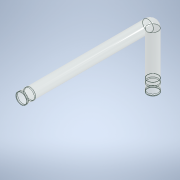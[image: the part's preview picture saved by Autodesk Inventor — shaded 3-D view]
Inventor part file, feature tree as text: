
AUTODESK INVENTOR PART (.ipt)
format: ipt  version: 2020 (Build 240168000, 168)  size: 269,312 bytes
history: native  units: mm
features: sketch x6, revolve x2, plane x2, sweep x1
ambient origin geometry x8: Origin, YZ Plane, XZ Plane, XY Plane, X Axis, Y Axis, Z Axis, Center Point
bodies: Solid1 (feature_tree), Solid2 (feature_tree)
feature tree (11):
  revolve  "Revolution1"  [1 undecoded]
  sweep  "Sweep1"
  sketch  "Sketch5"  dims[d14=11.5mm]
  sketch  "Sketch6"  dims[d15=0.5mm]
  plane  "Work Plane2"
  revolve  "Revolution2"  [1 undecoded]
  sketch  "Sketch2"  dims[d1=11.5mm d5=12.0mm]
  sketch  "Sketch3"  dims[d9=6.0mm d11=1.625mm]
  sketch  "Sketch4"  dims[d12=1.625mm d13=1.0mm]
  plane  "Work Plane1"
  sketch  "Sketch7"  dims[d16=90.0deg d17=23.0mm d18=100.0mm d19=250.0mm d20=10.0mm d21=0.0mm d22=0.0mm d23=-11.5mm d24=11.5mm d25=12.0mm d26=6.0mm d27=1.625mm d28=1.625mm d29=1.0mm d30=11.5mm d31=0.5mm d41=90.0deg]
note: 2 required parameter values undecoded (feature->parameter linkage not recoverable at this tier; creation-order binding heuristic only, values carry confidence <= 0.55)
